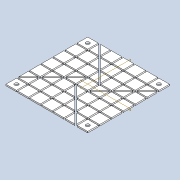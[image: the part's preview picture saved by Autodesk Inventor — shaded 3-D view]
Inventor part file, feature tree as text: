
AUTODESK INVENTOR PART (.ipt)
format: ipt  version: 2022 (Build 260153000, 153)  size: 333,824 bytes
history: native  units: in
note: dims shown in document units (in); Inventor stores cm internally (conversion verified against a paired STEP export)
features: extrude x2, plane x2, sketch x1, other x1, pattern_circular x1
ambient origin geometry x8: Origin, YZ Plane, XZ Plane, XY Plane, X Axis, Y Axis, Z Axis, Center Point
bodies: Solid1 (feature_tree)
feature tree (7):
  sketch  "Sketch1"  dims[d0=3.75in d1=3.75in d2=3.1496in d4=0.5357in d5=3.1496in d7=0.5357in d10=0.0312in d11=0.0312in d12=0.0312in d13=0.0312in d14=0.0312in d15=0.0312in d16=0.0312in d17=0.0312in d18=0.0312in d19=0.0312in d20=0.0312in d21=0.0312in d22=0.0312in d23=0.0312in d24=0.0312in d25=0.0312in d26=0.0312in d27=0.0312in d28=0.0312in d29=0.0625in d30=0.0in d31=0.0625in d32=0.0in d33=1.5748in d34=360.0deg d36=0.17in d37=0.2679in d38=0.2679in]
  extrude  "Extrusion1"  Depth=0.0625in
  extrude  "Extrusion2"  Depth=0.5357in
  other  "Work Axis1"
  pattern_circular  "Circular Pattern1"  [2 undecoded]
  plane  "Work Plane1"
  plane  "Work Plane2"
note: 2 required parameter values undecoded (feature->parameter linkage not recoverable at this tier; creation-order binding heuristic only, values carry confidence <= 0.55)
